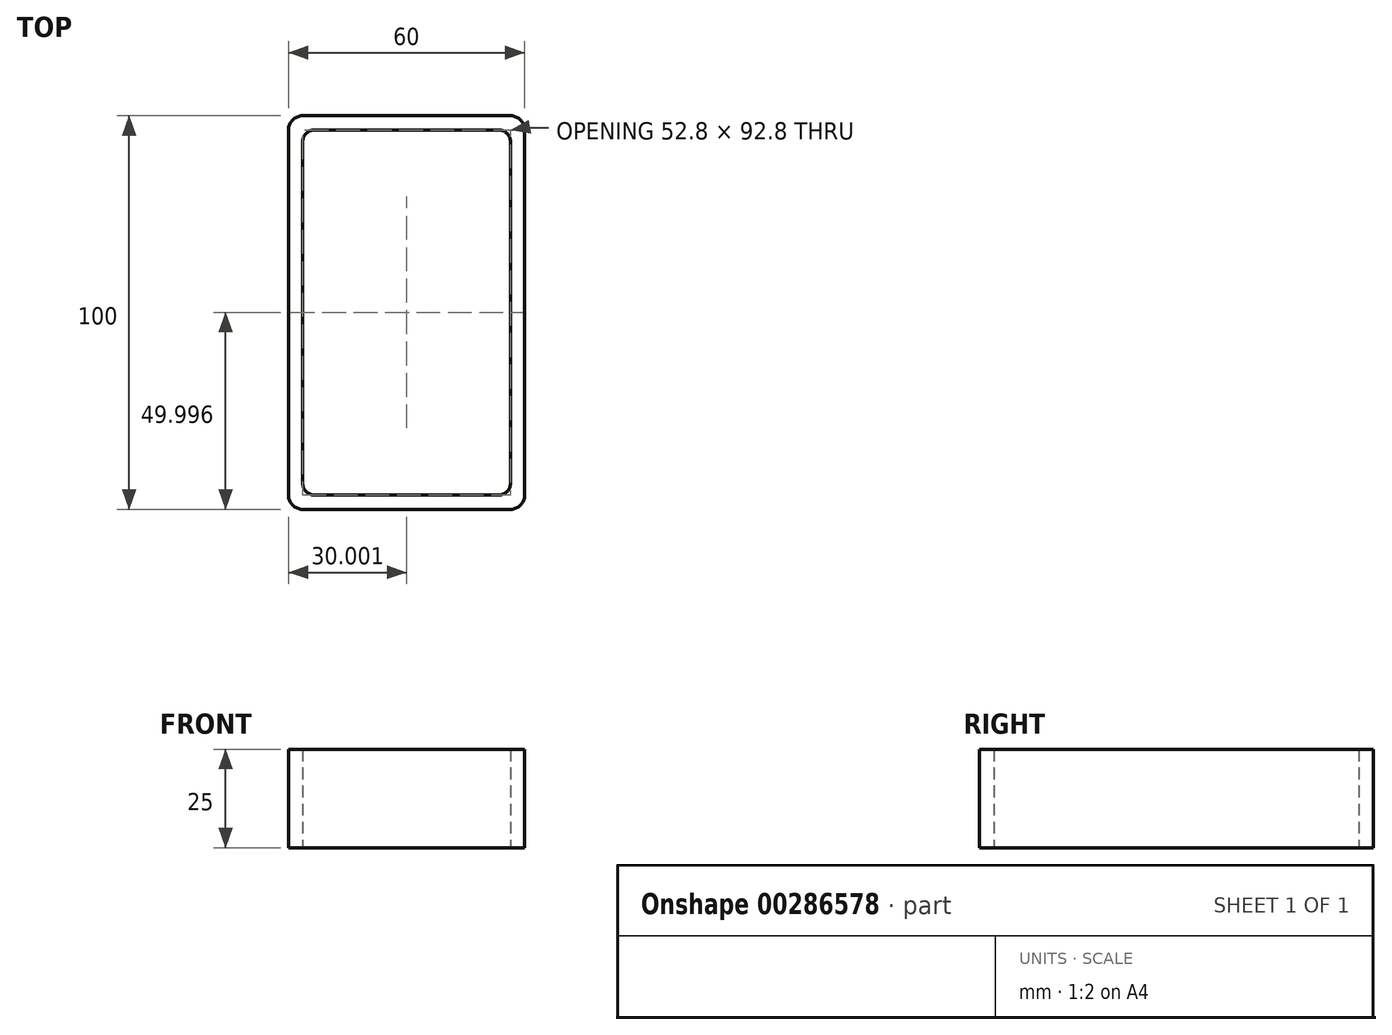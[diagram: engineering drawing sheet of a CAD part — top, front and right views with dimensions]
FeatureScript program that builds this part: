
annotation { "Feature Type Name" : "Feature", "Feature Type Description" : "" }
export const myFeature = defineFeature(function(context is Context, id is Id, definition is map)
    precondition{}
    {
        {
            var Q0;
            Q0=qCreatedBy(makeId("Top.planeOp"),FACE);
            var sketch = newSketch(context, id + "F0", { "sketchPlane" : qUnion([Q0])});
            skLineSegment(sketch, "E0", {"start": v(-55.85, 78.76) * mm, "end": v(-3.05, 78.76) * mm});
            skLineSegment(sketch, "E1", {"start": v(0.55, 75.16) * mm, "end": v(0.55, -17.64) * mm});
            skLineSegment(sketch, "E2", {"start": v(-3.05, -21.24) * mm, "end": v(-55.85, -21.24) * mm});
            skLineSegment(sketch, "E3", {"start": v(-59.45, -17.64) * mm, "end": v(-59.45, 75.16) * mm});
            skPoint(sketch, "E4.visualSharp", {"position": v(-59.45, -21.24) * mm});
            skArc(sketch, "E4.filletArc", {"start": v(-59.45, -17.64) * mm, "mid": v(-58.4, -20.19) * mm, "end": v(-55.85, -21.24) * mm});
            skPoint(sketch, "E5.visualSharp", {"position": v(0.55, -21.24) * mm});
            skArc(sketch, "E5.filletArc", {"start": v(-3.05, -21.24) * mm, "mid": v(-0.5, -20.19) * mm, "end": v(0.55, -17.64) * mm});
            skPoint(sketch, "E6.visualSharp", {"position": v(0.55, 78.76) * mm});
            skArc(sketch, "E6.filletArc", {"start": v(0.55, 75.16) * mm, "mid": v(-0.5, 77.7) * mm, "end": v(-3.05, 78.76) * mm});
            skPoint(sketch, "E7.visualSharp", {"position": v(-59.45, 78.76) * mm});
            skArc(sketch, "E7.filletArc", {"start": v(-55.85, 78.76) * mm, "mid": v(-58.4, 77.7) * mm, "end": v(-59.45, 75.16) * mm});
            skLineSegment(sketch, "E8", {"start": v(-6.05, 75.16) * mm, "end": v(-52.85, 75.16) * mm});
            skLineSegment(sketch, "E9", {"start": v(-55.85, -14.64) * mm, "end": v(-55.85, 72.16) * mm});
            skLineSegment(sketch, "E10", {"start": v(-52.85, -17.64) * mm, "end": v(-6.05, -17.64) * mm});
            skLineSegment(sketch, "E11", {"start": v(-3.05, 72.16) * mm, "end": v(-3.05, -14.64) * mm});
            skArc(sketch, "E12.filletArc", {"start": v(-55.85, -14.64) * mm, "mid": v(-54.97, -16.77) * mm, "end": v(-52.85, -17.64) * mm});
            skArc(sketch, "E13.filletArc", {"start": v(-6.05, -17.64) * mm, "mid": v(-3.93, -16.77) * mm, "end": v(-3.05, -14.64) * mm});
            skArc(sketch, "E14.filletArc", {"start": v(-3.05, 72.16) * mm, "mid": v(-3.93, 74.28) * mm, "end": v(-6.05, 75.16) * mm});
            skArc(sketch, "E15.filletArc", {"start": v(-52.85, 75.16) * mm, "mid": v(-54.97, 74.28) * mm, "end": v(-55.85, 72.16) * mm});
            skSolve(sketch);
        }
        {
            var Q0;
            Q0=makeQuery(id+"F0.imprint","IMPRINT",FACE,{"disambiguationData":[TD([[makeQuery(id+"F0.imprint","IMPRINT",EDGE,{"derivedFrom":sQuery(id+"F0.wireOp",EDGE,"E0")}),-1.0]])]});
            extrude(context, id + "F1", {"entities" : qUnion([Q0]), "depth" : 25 * mm});
        }
    });
